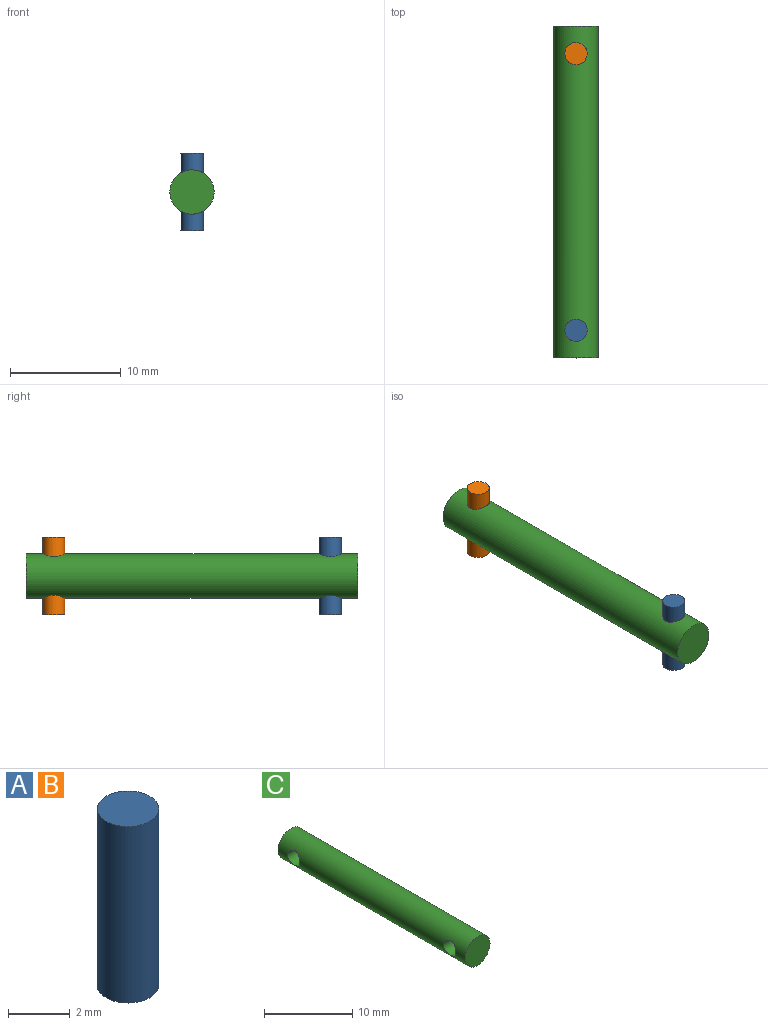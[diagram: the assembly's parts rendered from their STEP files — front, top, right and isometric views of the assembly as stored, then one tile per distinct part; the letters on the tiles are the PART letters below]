
ASSEMBLY  parts=3 mates=2
PART A: 3 faces, bbox 2x2x7 mm
  f0: cylinder r=1mm len=7mm, axis (0,0,-1), area 44mm2, adj f1,f2
  f1: plane 2x2mm, normal (0,0,1), area 3.1mm2, adj f0
  f2: plane 2x2mm, normal (0,0,-1), area 3.1mm2, adj f0
PART B: same geometry as A
PART C: 5 faces, bbox 4x30x4 mm
  f0: cylinder r=2mm len=30mm, axis (0,1,0), area 364mm2, adj f1,f2,f3,f4
  f1: plane 4x4mm, normal (0,-1,0), area 12.6mm2, adj f0
  f2: plane 4x4mm, normal (0,1,0), area 12.6mm2, adj f0
  f3: cylinder r=1mm len=4mm, axis (1,0,0), area 23.5mm2, adj f0
  f4: cylinder r=1mm len=4mm, axis (1,0,0), area 23.5mm2, adj f0
PLACE A t=(-51.25,17.55,-12.47)mm
PLACE B t=(-51.25,42.55,-12.47)mm
PLACE C rot(axis=(0,1,0),90deg) t=(-0.69,21.12,-8.97)mm
MATE fastened B.f0 <-> C.f3  axis (0,0,-1) through (-0.69,18.62,-8.97)mm
MATE fastened C.f4 <-> A.f0  axis (0,0,-1) through (-0.69,-6.38,-8.97)mm
